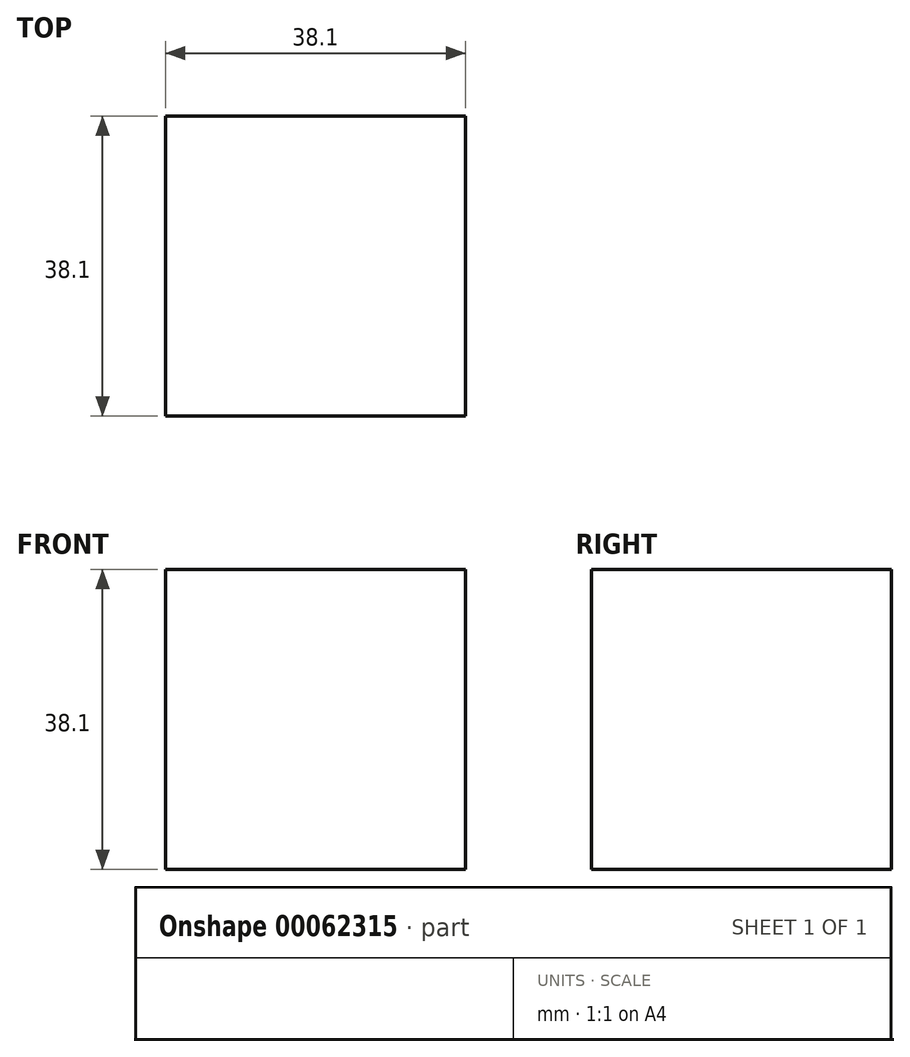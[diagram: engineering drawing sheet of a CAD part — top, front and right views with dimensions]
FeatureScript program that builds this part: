
annotation { "Feature Type Name" : "Feature", "Feature Type Description" : "" }
export const myFeature = defineFeature(function(context is Context, id is Id, definition is map)
    precondition{}
    {
        {
            var Q0;
            Q0=qCreatedBy(makeId("Front.planeOp"),FACE);
            var sketch = newSketch(context, id + "F0", { "sketchPlane" : qUnion([Q0])});
            skLineSegment(sketch, "E0", {"start": v(0, 0) * mm, "end": v(0, 38.1) * mm});
            skLineSegment(sketch, "E1", {"start": v(0, 38.1) * mm, "end": v(38.1, 38.1) * mm});
            skLineSegment(sketch, "E2", {"start": v(38.1, 38.1) * mm, "end": v(38.1, 0) * mm});
            skLineSegment(sketch, "E3", {"start": v(38.1, 0) * mm, "end": v(0, 0) * mm});
            skSolve(sketch);
        }
        {
            var Q0;
            Q0=makeQuery(id+"F0.imprint","IMPRINT",FACE,{"disambiguationData":[TD([[makeQuery(id+"F0.imprint","IMPRINT",EDGE,{"derivedFrom":sQuery(id+"F0.wireOp",EDGE,"E0")}),-1.0]])]});
            extrude(context, id + "F1", {"entities" : qUnion([Q0]), "oppositeDirection" : true, "depth" : 38.1 * mm});
        }
    });
